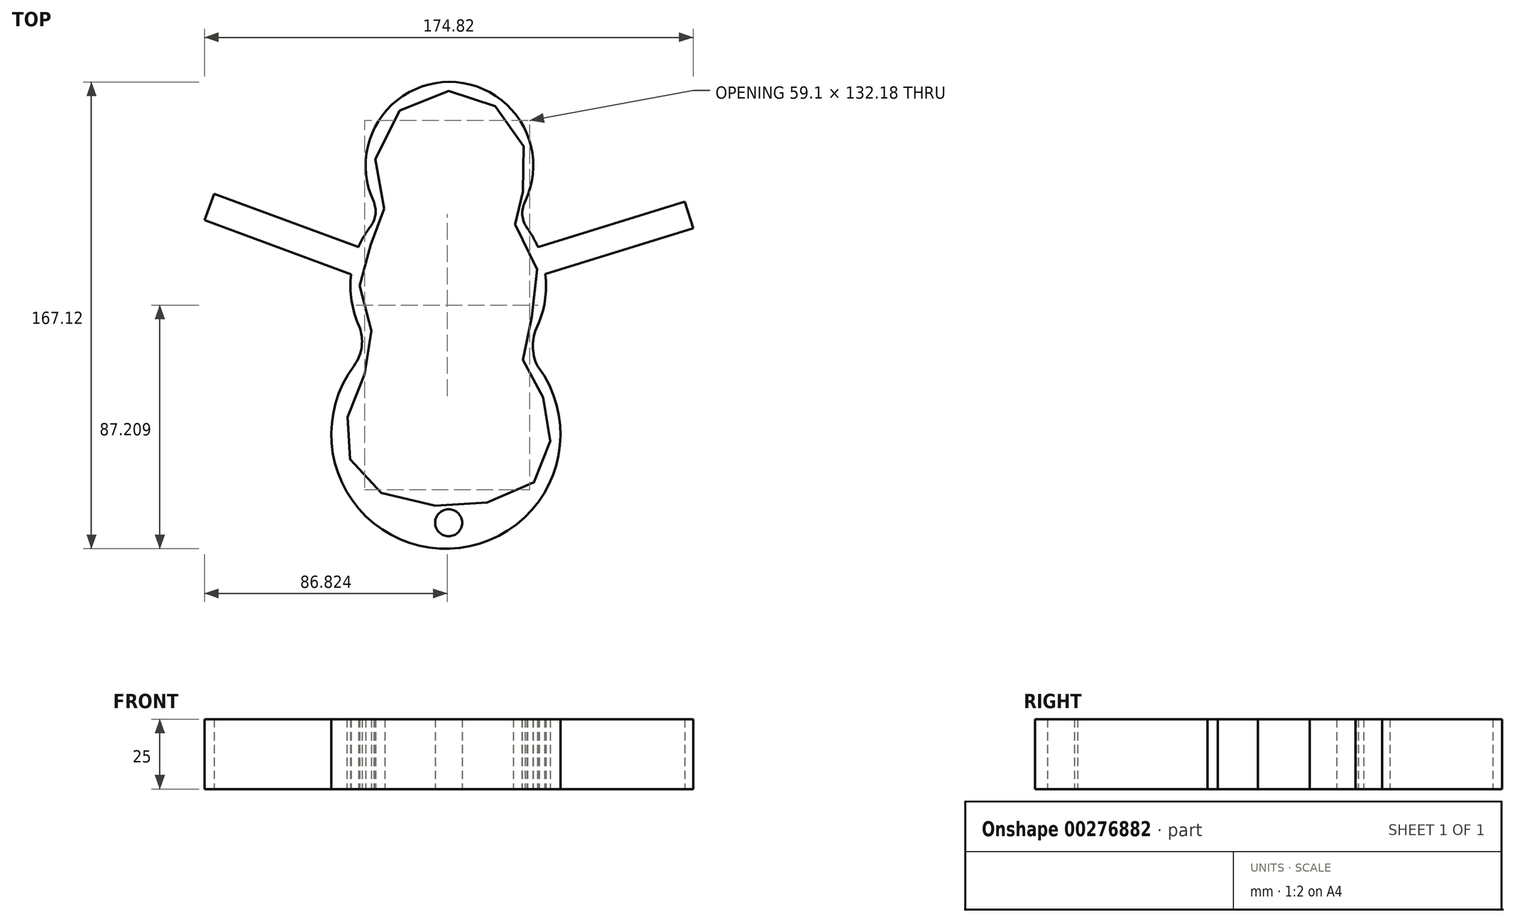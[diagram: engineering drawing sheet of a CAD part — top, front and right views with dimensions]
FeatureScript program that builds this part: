
annotation { "Feature Type Name" : "Feature", "Feature Type Description" : "" }
export const myFeature = defineFeature(function(context is Context, id is Id, definition is map)
    precondition{}
    {
        {
            var Q0;
            Q0=qCreatedBy(makeId("Top.planeOp"),FACE);
            var sketch = newSketch(context, id + "F0", { "sketchPlane" : qUnion([Q0])});
            skArc(sketch, "E0", {"start": v(22.72, 30.15) * mm, "mid": v(-4.38, 73.02) * mm, "end": v(-31.48, 30.15) * mm});
            skArc(sketch, "E1", {"start": v(-32.32, 21.62) * mm, "mid": v(-39.62, 3.48) * mm, "end": v(-36.05, -15.75) * mm});
            skArc(sketch, "E2", {"start": v(-38.54, -28.6) * mm, "mid": v(-7.88, -94.04) * mm, "end": v(29.68, -32.3) * mm});
            skPoint(sketch, "E3", {"position": v(-33.29, 35) * mm});
            skPoint(sketch, "E4", {"position": v(-34, 19.28) * mm});
            skPoint(sketch, "E5", {"position": v(-37.48, -12.51) * mm});
            skPoint(sketch, "E6", {"position": v(-38.54, -28.6) * mm});
            skPoint(sketch, "E7", {"position": v(22.22, 29.15) * mm});
            skPoint(sketch, "E8", {"position": v(22.97, 21.3) * mm});
            skPoint(sketch, "E9", {"position": v(28.5, -10.81) * mm});
            skPoint(sketch, "E10", {"position": v(29.63, -32.23) * mm});
            skArc(sketch, "E11.trimOffspring", {"start": v(27.16, -14.29) * mm, "mid": v(30, 3.78) * mm, "end": v(23.35, 20.8) * mm});
            skPoint(sketch, "E12.visualSharp", {"position": v(-29.35, 26.4) * mm});
            skPoint(sketch, "E13.visualSharp", {"position": v(-34.05, -19.21) * mm});
            skPoint(sketch, "E14.visualSharp", {"position": v(-36.44, -26.01) * mm});
            skPoint(sketch, "E15.visualSharp", {"position": v(25.4, -17.7) * mm});
            skPoint(sketch, "E16.visualSharp", {"position": v(25.77, -26.77) * mm});
            skLineSegment(sketch, "E16.filletArc", {"start": v(29.68, -32.3) * mm, "end": v(29.68, -32.3) * mm});
            skPoint(sketch, "E17.visualSharp", {"position": v(21.46, 27.78) * mm});
            skArc(sketch, "E18.filletArc", {"start": v(23.07, 21.23) * mm, "mid": v(23.2, 21.01) * mm, "end": v(23.35, 20.8) * mm});
            skArc(sketch, "E19", {"start": v(22.72, 30.15) * mm, "mid": v(21.72, 25.4) * mm, "end": v(23.35, 20.8) * mm});
            skPoint(sketch, "E20.startSnap0", {"position": v(21.72, 25.4) * mm});
            skLineSegment(sketch, "E21", {"start": v(-34.98, -20.44) * mm, "end": v(-34.9, -20.44) * mm});
            skPoint(sketch, "E21.startSnap0", {"position": v(-34.98, -21.2) * mm});
            skPoint(sketch, "E21.endSnap0", {"position": v(39.7, -20.44) * mm});
            skPoint(sketch, "E20.start.orphan", {"position": v(21.72, 26.6) * mm});
            skArc(sketch, "E22", {"start": v(-32.94, 20.8) * mm, "mid": v(-30.88, 25.27) * mm, "end": v(-31.48, 30.15) * mm});
            skArc(sketch, "E23", {"start": v(27.16, -14.29) * mm, "mid": v(25.44, -21.5) * mm, "end": v(27.17, -28.7) * mm});
            skArc(sketch, "E24", {"start": v(-34.9, -20.44) * mm, "mid": v(-35.5, -17.27) * mm, "end": v(-36.75, -14.29) * mm});
            skArc(sketch, "E25", {"start": v(-38.54, -28.6) * mm, "mid": v(-35.76, -21.68) * mm, "end": v(-36.75, -14.29) * mm});
            skPoint(sketch, "E26.trimOffspring.end.orphan", {"position": v(25.4, -20.44) * mm});
            skPoint(sketch, "E27.end.orphan", {"position": v(29.68, -27.28) * mm});
            skArc(sketch, "E28", {"start": v(27.17, -28.7) * mm, "mid": v(28.41, -30.5) * mm, "end": v(29.68, -32.3) * mm});
            skFitSpline(sketch, "E29", {"points": [v(-34.71, -31.53) * mm, v(-40.1, -43.25) * mm, v(-41.05, -53.62) * mm, v(-39.33, -63.8) * mm, v(-31.06, -72.84) * mm, v(-14.73, -78.02) * mm, v(2.17, -78.6) * mm, v(16, -75.53) * mm, v(28.3, -67.84) * mm, v(31.57, -56.9) * mm, v(31, -45.75) * mm, v(26.76, -34.99) * mm, v(21.96, -26.34) * mm, v(23.3, -14.82) * mm, v(27.34, -5.4) * mm, v(25.4, 10.93) * mm, v(19.08, 22.26) * mm, v(19.27, 28.8) * mm, v(22.72, 35.52) * mm, v(22.72, 48.2) * mm, v(16.39, 60.3) * mm, v(4.48, 68.37) * mm, v(-9.36, 69.14) * mm, v(-23.96, 61.07) * mm, v(-30.87, 45.32) * mm, v(-28.37, 30.15) * mm, v(-28, 21.5) * mm, v(-33.75, 13.04) * mm, v(-36.44, 3.24) * mm, v(-35.1, -8.86) * mm, v(-31.26, -20.44) * mm, v(-34.71, -31.53) * mm]});
            skCircle(sketch, "E30", {"center": v(-4.64, -84.78) * mm, "radius": 4.83 * mm});
            skCircle(sketch, "E31", {"center": v(-12.9, 51.73) * mm, "radius": 5 * mm});
            skCircle(sketch, "E32", {"center": v(1.28, 52.25) * mm, "radius": 5 * mm});
            skArc(sketch, "E33", {"start": v(-14.48, 40.63) * mm, "mid": v(-4.08, 35.42) * mm, "end": v(6.28, 40.7) * mm});
            skArc(sketch, "E34", {"start": v(-14.48, 40.63) * mm, "mid": v(-4.1, 38.48) * mm, "end": v(6.28, 40.7) * mm});
            skLineSegment(sketch, "E35", {"start": v(27.34, 13.86) * mm, "end": v(79.86, 30.2) * mm});
            skLineSegment(sketch, "E36", {"start": v(79.86, 30.2) * mm, "end": v(82.83, 20.65) * mm});
            skLineSegment(sketch, "E37", {"start": v(82.83, 20.65) * mm, "end": v(29.95, 4.2) * mm});
            skLineSegment(sketch, "E38", {"start": v(-36.94, 13.86) * mm, "end": v(-88.52, 32.94) * mm});
            skLineSegment(sketch, "E39", {"start": v(-88.52, 32.94) * mm, "end": v(-91.99, 23.56) * mm});
            skLineSegment(sketch, "E40", {"start": v(-91.99, 23.56) * mm, "end": v(-39.55, 4.16) * mm});
            skLineSegment(sketch, "E41", {"start": v(-15.44, 56.03) * mm, "end": v(-16.96, 58.01) * mm});
            skLineSegment(sketch, "E42", {"start": v(-13.36, 56.7) * mm, "end": v(-13.36, 59.2) * mm});
            skLineSegment(sketch, "E43", {"start": v(-13.36, 59.2) * mm, "end": v(-13.36, 56.7) * mm});
            skPoint(sketch, "E44.endSnap0", {"position": v(-2.55, 56.95) * mm});
            skCircle(sketch, "E45", {"center": v(-12.9, 51.73) * mm, "radius": 1.96 * mm});
            skCircle(sketch, "E46", {"center": v(1.28, 52.25) * mm, "radius": 1.94 * mm});
            skPoint(sketch, "E47.end.orphan", {"position": v(-6.89, 58.01) * mm});
            skLineSegment(sketch, "E48", {"start": v(-9.73, 55.6) * mm, "end": v(-9.1, 58.01) * mm});
            skPoint(sketch, "E49.end.orphan", {"position": v(7.65, 58.01) * mm});
            skPoint(sketch, "E44.start.orphan", {"position": v(-2.95, 58.01) * mm});
            skPoint(sketch, "E50.start.orphan", {"position": v(-2.16, 55.88) * mm});
            skPoint(sketch, "E51.start.orphan", {"position": v(-0.98, 56.7) * mm});
            skLineSegment(sketch, "E52", {"start": v(1.46, 57.24) * mm, "end": v(1.46, 59.74) * mm});
            skPoint(sketch, "E53.end.orphan", {"position": v(-2.55, 58.2) * mm});
            skPoint(sketch, "E53.start.orphan", {"position": v(-2.43, 55.6) * mm});
            skPoint(sketch, "E54.end.orphan", {"position": v(7.29, 58.2) * mm});
            skPoint(sketch, "E54.start.orphan", {"position": v(4.99, 55.6) * mm});
            skLineSegment(sketch, "E55", {"start": v(4.82, 55.77) * mm, "end": v(6.73, 57.39) * mm});
            skPoint(sketch, "E56.end.orphan", {"position": v(-3.1, 58.01) * mm});
            skLineSegment(sketch, "E57", {"start": v(-0.98, 56.7) * mm, "end": v(-2.55, 58.65) * mm});
            skSolve(sketch);
        }
        {
            var Q0;
            Q0 = qSketchRegion(id + "F0", true);
            extrude(context, id + "F1", {"entities" : qUnion([Q0]), "depth" : 25 * mm});
        }
    });
